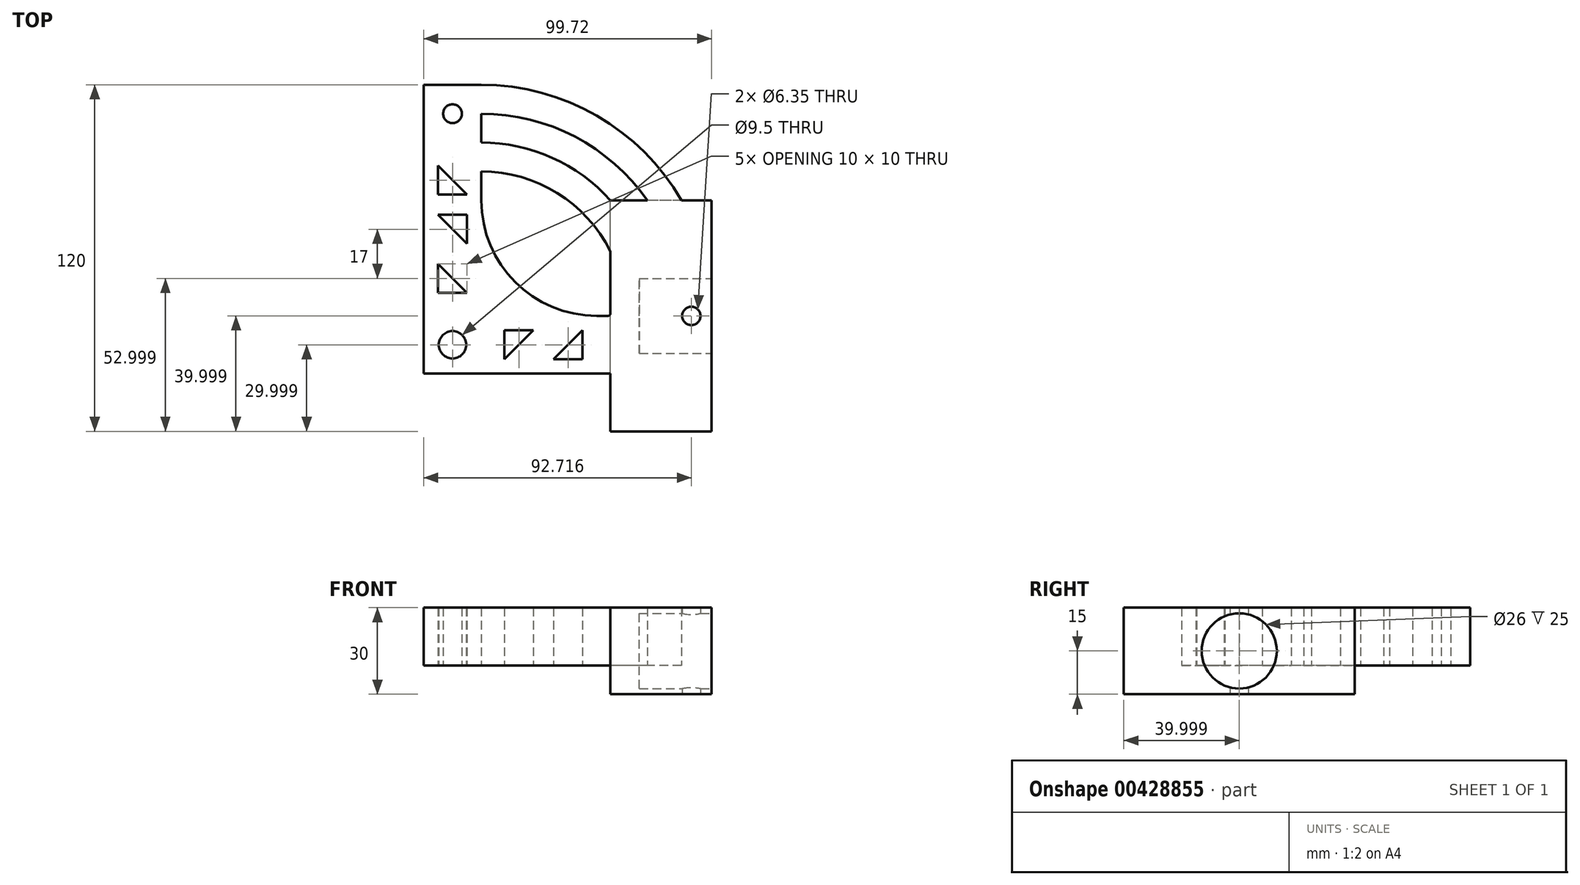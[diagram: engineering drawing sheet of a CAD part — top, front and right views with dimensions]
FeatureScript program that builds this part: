
annotation { "Feature Type Name" : "Feature", "Feature Type Description" : "" }
export const myFeature = defineFeature(function(context is Context, id is Id, definition is map)
    precondition{}
    {
        {
            var Q0;
            Q0=qCreatedBy(makeId("Top.planeOp"),FACE);
            var sketch = newSketch(context, id + "F0", { "sketchPlane" : qUnion([Q0])});
            skLineSegment(sketch, "E0.bottom", {"start": v(-8.64, 71.98) * mm, "end": v(-28.64, 71.98) * mm});
            skLineSegment(sketch, "E0.top", {"start": v(-8.64, -28.02) * mm, "end": v(-28.64, -28.02) * mm});
            skLineSegment(sketch, "E0.left", {"start": v(-8.64, 71.98) * mm, "end": v(-8.64, 31.98) * mm});
            skLineSegment(sketch, "E0.right", {"start": v(-28.64, 71.98) * mm, "end": v(-28.64, -28.02) * mm});
            skLineSegment(sketch, "E1.bottom", {"start": v(31.36, -8.02) * mm, "end": v(35.08, -8.02) * mm});
            skLineSegment(sketch, "E1.top", {"start": v(-8.64, -28.02) * mm, "end": v(35.08, -28.02) * mm});
            skLineSegment(sketch, "E1.left", {"start": v(-8.64, -8.02) * mm, "end": v(-8.64, -28.02) * mm});
            skCircle(sketch, "E2", {"center": v(-18.64, -18.02) * mm, "radius": 4.75 * mm});
            skLineSegment(sketch, "E3", {"start": v(-13.64, 16.98) * mm, "end": v(-23.64, 26.98) * mm});
            skLineSegment(sketch, "E4", {"start": v(-23.64, 26.98) * mm, "end": v(-13.64, 26.98) * mm});
            skLineSegment(sketch, "E5", {"start": v(-13.64, 26.98) * mm, "end": v(-13.64, 16.98) * mm});
            skLineSegment(sketch, "E6", {"start": v(-23.64, 9.98) * mm, "end": v(-13.64, -0.02) * mm});
            skLineSegment(sketch, "E7", {"start": v(-13.64, -0.02) * mm, "end": v(-23.64, -0.02) * mm});
            skLineSegment(sketch, "E8", {"start": v(-23.64, -0.02) * mm, "end": v(-23.64, 9.98) * mm});
            skCircle(sketch, "E9", {"center": v(-18.64, 61.98) * mm, "radius": 3.25 * mm});
            skLineSegment(sketch, "E10", {"start": v(-23.64, 43.98) * mm, "end": v(-13.64, 33.98) * mm});
            skLineSegment(sketch, "E11", {"start": v(-13.64, 33.98) * mm, "end": v(-23.64, 33.98) * mm});
            skLineSegment(sketch, "E12", {"start": v(-23.64, 33.98) * mm, "end": v(-23.64, 43.98) * mm});
            skLineSegment(sketch, "E13", {"start": v(16.36, -23.02) * mm, "end": v(26.36, -13.02) * mm});
            skLineSegment(sketch, "E14", {"start": v(26.36, -13.02) * mm, "end": v(26.36, -23.02) * mm});
            skLineSegment(sketch, "E15", {"start": v(26.36, -23.02) * mm, "end": v(16.36, -23.02) * mm});
            skLineSegment(sketch, "E16", {"start": v(9.36, -13.02) * mm, "end": v(-0.64, -23.02) * mm});
            skLineSegment(sketch, "E17", {"start": v(-0.64, -23.02) * mm, "end": v(-0.64, -13.02) * mm});
            skLineSegment(sketch, "E18", {"start": v(-0.64, -13.02) * mm, "end": v(9.36, -13.02) * mm});
            skCircle(sketch, "E19", {"center": v(-8.64, -8.02) * mm, "radius": 80 * mm});
            skCircle(sketch, "E20", {"center": v(-8.64, -8.02) * mm, "radius": 70 * mm});
            skCircle(sketch, "E21", {"center": v(-8.64, -8.02) * mm, "radius": 60 * mm});
            skCircle(sketch, "E22", {"center": v(-8.64, -8.02) * mm, "radius": 50 * mm});
            skLineSegment(sketch, "E23.bottom", {"start": v(71.08, -48.02) * mm, "end": v(36.08, -48.02) * mm});
            skLineSegment(sketch, "E23.top", {"start": v(71.08, 31.98) * mm, "end": v(36.08, 31.98) * mm});
            skLineSegment(sketch, "E23.left", {"start": v(71.08, -48.02) * mm, "end": v(71.08, 31.98) * mm});
            skLineSegment(sketch, "E23.right", {"start": v(36.08, -7.02) * mm, "end": v(36.08, 31.98) * mm});
            skPoint(sketch, "E24", {"position": v(36.08, -8.02) * mm});
            skArc(sketch, "E25.filletArc", {"start": v(35.08, -8.02) * mm, "mid": v(35.78, -7.73) * mm, "end": v(36.08, -7.02) * mm});
            skLineSegment(sketch, "E26", {"start": v(36.08, -29.02) * mm, "end": v(36.08, -48.02) * mm});
            skLineSegment(sketch, "E27", {"start": v(36.08, -7.02) * mm, "end": v(36.08, -29.02) * mm});
            skArc(sketch, "E28.filletArc", {"start": v(-8.64, 31.98) * mm, "mid": v(3.07, 3.7) * mm, "end": v(31.36, -8.02) * mm});
            skLineSegment(sketch, "E29", {"start": v(35.08, -28.02) * mm, "end": v(36.08, -28.02) * mm});
            skCircle(sketch, "E30", {"center": v(64.08, -8.02) * mm, "radius": 3.18 * mm});
            skSolve(sketch);
        }
        {
            var Q0;
            {var subQ11=sQuery(id+"F0.wireOp",EDGE,"E0.top");Q0=makeQuery(id+"F0.imprint","IMPRINT",FACE,{"disambiguationData":[TD([[makeQuery(id+"F0.imprint","IMPRINT",EDGE,{"derivedFrom":subQ11}),-1.0]])]});}
            var Q1;
            {var subQ5=sQuery(id+"F0.wireOp",EDGE,"E21");var subQ6=sQuery(id+"F0.wireOp",EDGE,"E0.left");var subQ7=makeQuery(id+"F0.imprint","INTERSECT",VERTEX,{"derivedFrom":[subQ6,subQ5]});Q1=makeQuery(id+"F0.imprint","IMPRINT",FACE,{"disambiguationData":[TD([[makeQuery(id+"F0.imprint","IMPRINT",EDGE,{"disambiguationData":[TD([[subQ7,-1.0]])],"derivedFrom":subQ6}),-1.0]])]});}
            var Q2;
            {var subQ0=sQuery(id+"F0.wireOp",EDGE,"E20");var subQ1=sQuery(id+"F0.wireOp",EDGE,"E0.left");var subQ2=makeQuery(id+"F0.imprint","INTERSECT",VERTEX,{"derivedFrom":[subQ1,subQ0]});Q2=makeQuery(id+"F0.imprint","IMPRINT",FACE,{"disambiguationData":[TD([[makeQuery(id+"F0.imprint","IMPRINT",EDGE,{"disambiguationData":[TD([[subQ2,-1.0]])],"derivedFrom":subQ1}),-1.0]])]});}
            var Q3;
            {var subQ0=sQuery(id+"F0.wireOp",EDGE,"E19");var subQ3=sQuery(id+"F0.wireOp",EDGE,"E0.right");var subQ4=makeQuery(id+"F0.imprint","INTERSECT",VERTEX,{"derivedFrom":[subQ3,subQ0]});Q3=makeQuery(id+"F0.imprint","IMPRINT",FACE,{"disambiguationData":[TD([[makeQuery(id+"F0.imprint","IMPRINT",EDGE,{"disambiguationData":[TD([[subQ4,-1.0]])],"derivedFrom":subQ3}),1.0]])]});}
            var Q4;
            {var subQ0=sQuery(id+"F0.wireOp",EDGE,"E0.bottom");Q4=makeQuery(id+"F0.imprint","IMPRINT",FACE,{"disambiguationData":[TD([[makeQuery(id+"F0.imprint","IMPRINT",EDGE,{"derivedFrom":subQ0}),1.0]])]});}
            var Q5;
            {var subQ1=sQuery(id+"F0.wireOp",EDGE,"E0.left");var subQ3=sQuery(id+"F0.wireOp",EDGE,"E20");var subQ4=makeQuery(id+"F0.imprint","INTERSECT",VERTEX,{"derivedFrom":[subQ1,subQ3]});Q5=makeQuery(id+"F0.imprint","IMPRINT",FACE,{"disambiguationData":[TD([[makeQuery(id+"F0.imprint","IMPRINT",EDGE,{"disambiguationData":[TD([[subQ4,1.0]])],"derivedFrom":subQ3}),-1.0]])]});}
            var Q6;
            {var subQ0=sQuery(id+"F0.wireOp",EDGE,"E21");var subQ1=sQuery(id+"F0.wireOp",EDGE,"E0.left");var subQ2=makeQuery(id+"F0.imprint","INTERSECT",VERTEX,{"derivedFrom":[subQ1,subQ0]});Q6=makeQuery(id+"F0.imprint","IMPRINT",FACE,{"disambiguationData":[TD([[makeQuery(id+"F0.imprint","IMPRINT",EDGE,{"disambiguationData":[TD([[subQ2,-1.0]])],"derivedFrom":subQ1}),1.0]])]});}
            var Q7;
            {var subQ3=sQuery(id+"F0.wireOp",EDGE,"E23.right");var subQ5=sQuery(id+"F0.wireOp",EDGE,"E22");var subQ7=makeQuery(id+"F0.imprint","INTERSECT",VERTEX,{"derivedFrom":[subQ5,subQ3]});Q7=makeQuery(id+"F0.imprint","IMPRINT",FACE,{"disambiguationData":[TD([[makeQuery(id+"F0.imprint","IMPRINT",EDGE,{"disambiguationData":[TD([[subQ7,1.0]])],"derivedFrom":subQ5}),-1.0]])]});}
            var Q8;
            {var subQ3=sQuery(id+"F0.wireOp",EDGE,"E23.top");var subQ5=sQuery(id+"F0.wireOp",EDGE,"E20");var subQ6=makeQuery(id+"F0.imprint","INTERSECT",VERTEX,{"derivedFrom":[subQ5,subQ3]});Q8=makeQuery(id+"F0.imprint","IMPRINT",FACE,{"disambiguationData":[TD([[makeQuery(id+"F0.imprint","IMPRINT",EDGE,{"disambiguationData":[TD([[subQ6,1.0]])],"derivedFrom":subQ5}),1.0]])]});}
            var Q9;
            {var subQ5=sQuery(id+"F0.wireOp",EDGE,"E23.top");var subQ8=sQuery(id+"F0.wireOp",EDGE,"E19");var subQ9=makeQuery(id+"F0.imprint","INTERSECT",VERTEX,{"derivedFrom":[subQ8,subQ5]});Q9=makeQuery(id+"F0.imprint","IMPRINT",FACE,{"disambiguationData":[TD([[makeQuery(id+"F0.imprint","IMPRINT",EDGE,{"disambiguationData":[TD([[subQ9,1.0]])],"derivedFrom":subQ8}),1.0]])]});}
            var Q10;
            {var subQ0=sQuery(id+"F0.wireOp",EDGE,"E23.top");var subQ1=sQuery(id+"F0.wireOp",EDGE,"E19");var subQ2=makeQuery(id+"F0.imprint","INTERSECT",VERTEX,{"derivedFrom":[subQ1,subQ0]});Q10=makeQuery(id+"F0.imprint","IMPRINT",FACE,{"disambiguationData":[TD([[makeQuery(id+"F0.imprint","IMPRINT",EDGE,{"disambiguationData":[TD([[subQ2,1.0]])],"derivedFrom":subQ1}),-1.0]])]});}
            var Q11;
            {var subQ3=sQuery(id+"F0.wireOp",EDGE,"E22");var subQ5=sQuery(id+"F0.wireOp",EDGE,"E23.right");var subQ8=makeQuery(id+"F0.imprint","INTERSECT",VERTEX,{"derivedFrom":[subQ3,subQ5]});Q11=makeQuery(id+"F0.imprint","IMPRINT",FACE,{"disambiguationData":[TD([[makeQuery(id+"F0.imprint","IMPRINT",EDGE,{"disambiguationData":[TD([[subQ8,1.0]])],"derivedFrom":subQ3}),1.0]])]});}
            var Q12;
            {var subQ0=sQuery(id+"F0.wireOp",EDGE,"E23.bottom");var subQ1=sQuery(id+"F0.wireOp",EDGE,"E19");var subQ2=makeQuery(id+"F0.imprint","INTERSECT",VERTEX,{"derivedFrom":[subQ1,subQ0]});Q12=makeQuery(id+"F0.imprint","IMPRINT",FACE,{"disambiguationData":[TD([[makeQuery(id+"F0.imprint","IMPRINT",EDGE,{"disambiguationData":[TD([[subQ2,-1.0]])],"derivedFrom":subQ1}),-1.0]])]});}
            extrude(context, id + "F1", {"entities" : qUnion([Q0, Q1, Q2, Q3, Q4, Q5, Q6, Q7, Q8, Q9, Q10, Q11, Q12]), "depth" : 20 * mm});
        }
        {
            var Q0;
            {var subQ3=sQuery(id+"F0.wireOp",EDGE,"E22");var subQ5=sQuery(id+"F0.wireOp",EDGE,"E23.right");var subQ8=makeQuery(id+"F0.imprint","INTERSECT",VERTEX,{"derivedFrom":[subQ3,subQ5]});Q0=makeQuery(id+"F0.imprint","IMPRINT",FACE,{"disambiguationData":[TD([[makeQuery(id+"F0.imprint","IMPRINT",EDGE,{"disambiguationData":[TD([[subQ8,1.0]])],"derivedFrom":subQ3}),1.0]])]});}
            var Q1;
            {var subQ3=sQuery(id+"F0.wireOp",EDGE,"E23.right");var subQ5=sQuery(id+"F0.wireOp",EDGE,"E22");var subQ7=makeQuery(id+"F0.imprint","INTERSECT",VERTEX,{"derivedFrom":[subQ5,subQ3]});Q1=makeQuery(id+"F0.imprint","IMPRINT",FACE,{"disambiguationData":[TD([[makeQuery(id+"F0.imprint","IMPRINT",EDGE,{"disambiguationData":[TD([[subQ7,1.0]])],"derivedFrom":subQ5}),-1.0]])]});}
            var Q2;
            {var subQ3=sQuery(id+"F0.wireOp",EDGE,"E23.top");var subQ5=sQuery(id+"F0.wireOp",EDGE,"E20");var subQ6=makeQuery(id+"F0.imprint","INTERSECT",VERTEX,{"derivedFrom":[subQ5,subQ3]});Q2=makeQuery(id+"F0.imprint","IMPRINT",FACE,{"disambiguationData":[TD([[makeQuery(id+"F0.imprint","IMPRINT",EDGE,{"disambiguationData":[TD([[subQ6,1.0]])],"derivedFrom":subQ5}),1.0]])]});}
            var Q3;
            {var subQ5=sQuery(id+"F0.wireOp",EDGE,"E23.top");var subQ8=sQuery(id+"F0.wireOp",EDGE,"E19");var subQ9=makeQuery(id+"F0.imprint","INTERSECT",VERTEX,{"derivedFrom":[subQ8,subQ5]});Q3=makeQuery(id+"F0.imprint","IMPRINT",FACE,{"disambiguationData":[TD([[makeQuery(id+"F0.imprint","IMPRINT",EDGE,{"disambiguationData":[TD([[subQ9,1.0]])],"derivedFrom":subQ8}),1.0]])]});}
            var Q4;
            {var subQ0=sQuery(id+"F0.wireOp",EDGE,"E23.top");var subQ1=sQuery(id+"F0.wireOp",EDGE,"E19");var subQ2=makeQuery(id+"F0.imprint","INTERSECT",VERTEX,{"derivedFrom":[subQ1,subQ0]});Q4=makeQuery(id+"F0.imprint","IMPRINT",FACE,{"disambiguationData":[TD([[makeQuery(id+"F0.imprint","IMPRINT",EDGE,{"disambiguationData":[TD([[subQ2,1.0]])],"derivedFrom":subQ1}),-1.0]])]});}
            var Q5;
            {var subQ0=sQuery(id+"F0.wireOp",EDGE,"E23.bottom");var subQ1=sQuery(id+"F0.wireOp",EDGE,"E19");var subQ2=makeQuery(id+"F0.imprint","INTERSECT",VERTEX,{"derivedFrom":[subQ1,subQ0]});Q5=makeQuery(id+"F0.imprint","IMPRINT",FACE,{"disambiguationData":[TD([[makeQuery(id+"F0.imprint","IMPRINT",EDGE,{"disambiguationData":[TD([[subQ2,-1.0]])],"derivedFrom":subQ1}),-1.0]])]});}
            extrude(context, id + "F2", {"entities" : qUnion([Q0, Q1, Q2, Q3, Q4, Q5]), "operationType" : NewBodyOperationType.ADD, "oppositeDirection" : true, "depth" : 10 * mm});
        }
        {
            var Q0;
            {var subQ0=sQuery(id+"F0.wireOp",EDGE,"E23.left");Q0=makeQuery(id+"F2.boolean.opBoolean","MERGE",FACE,{"derivedFrom":[makeQuery(id+"F1.opExtrude","SWEPT_FACE",FACE,{"disambiguationData":[OSD([subQ0])]}),makeQuery(id+"F2.opExtrude","SWEPT_FACE",FACE,{"disambiguationData":[OSD([subQ0])]})]});}
            var sketch = newSketch(context, id + "F3", { "sketchPlane" : qUnion([Q0])});
            skCircle(sketch, "E31", {"center": v(-8.02, 5) * mm, "radius": 13 * mm});
            skSolve(sketch);
        }
        {
            var Q0;
            Q0 = qSketchRegion(id + "F3", true);
            extrude(context, id + "F4", {"entities" : qUnion([Q0]), "operationType" : NewBodyOperationType.REMOVE, "oppositeDirection" : true, "depth" : 25 * mm});
        }
    });
